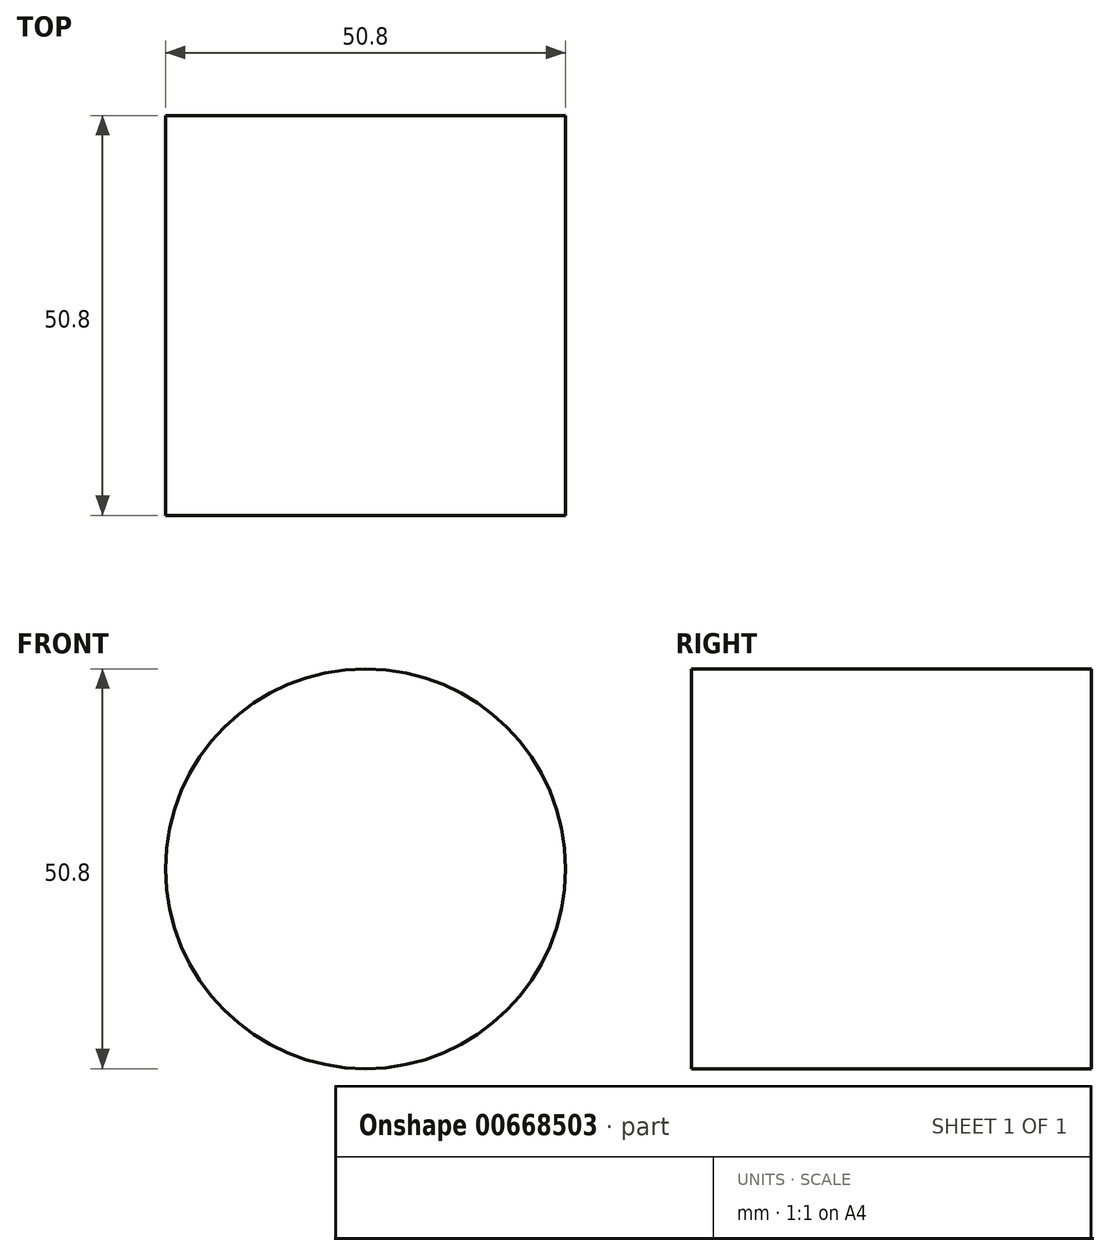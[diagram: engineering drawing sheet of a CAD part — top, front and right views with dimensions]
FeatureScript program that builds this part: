
annotation { "Feature Type Name" : "Feature", "Feature Type Description" : "" }
export const myFeature = defineFeature(function(context is Context, id is Id, definition is map)
    precondition{}
    {
        {
            var Q0;
            Q0=qCreatedBy(makeId("Front.planeOp"),FACE);
            var sketch = newSketch(context, id + "F0", { "sketchPlane" : qUnion([Q0])});
            skCircle(sketch, "E0", {"center": v(0, 0) * mm, "radius": 25.4 * mm});
            skSolve(sketch);
        }
        {
            var Q0;
            Q0 = qSketchRegion(id + "F0", false);
            extrude(context, id + "F1", {"entities" : qUnion([Q0]), "depth" : 50.8 * mm});
        }
    });
